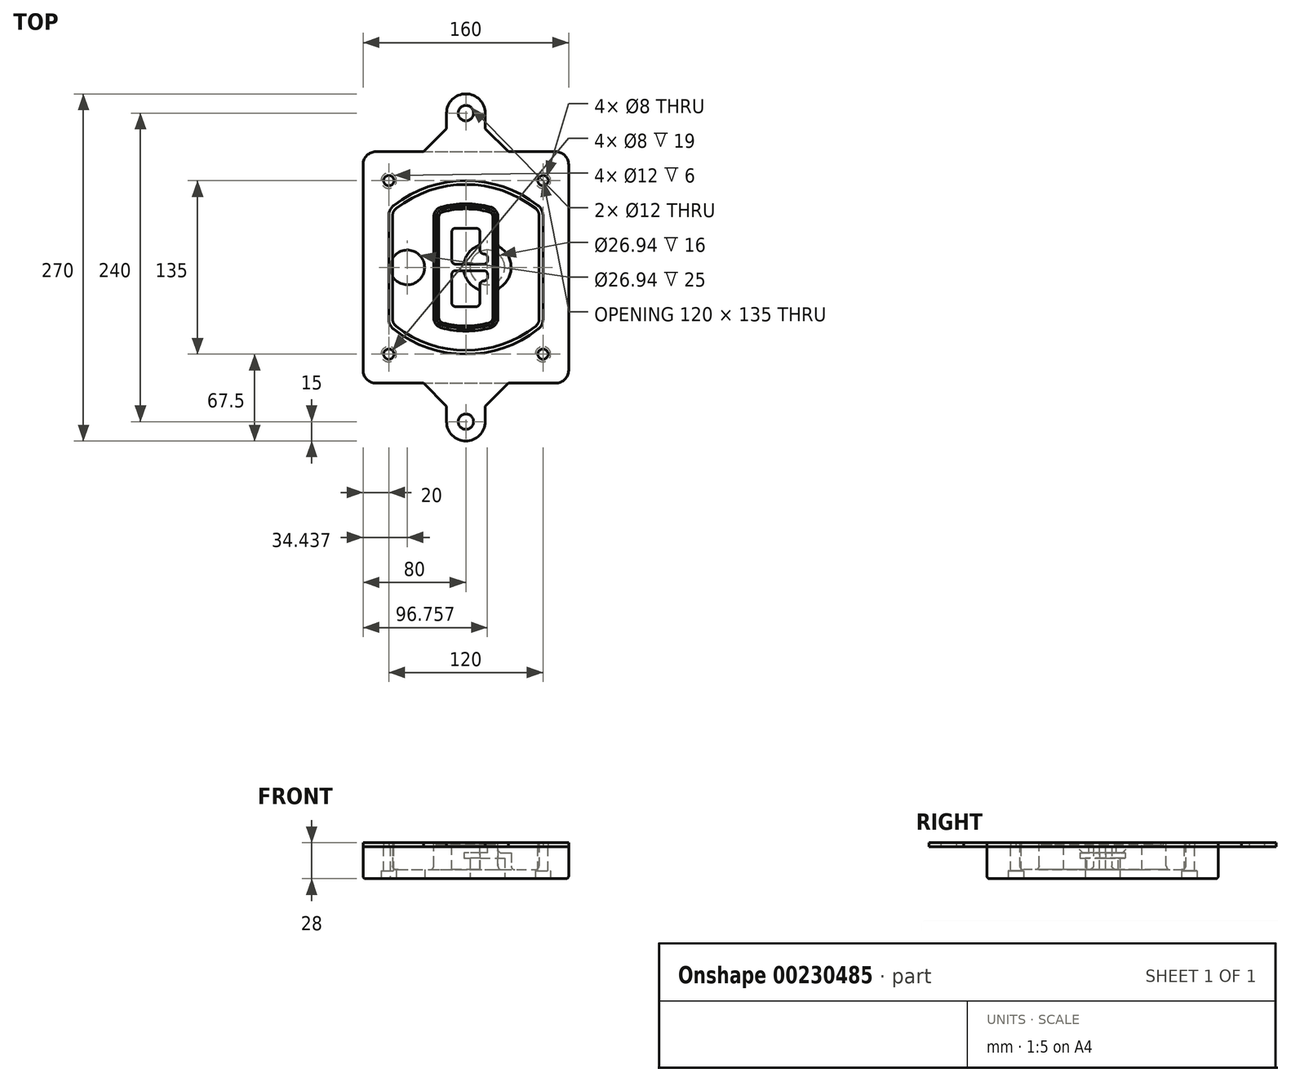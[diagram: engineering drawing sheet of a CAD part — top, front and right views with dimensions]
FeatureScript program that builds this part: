
annotation { "Feature Type Name" : "Feature", "Feature Type Description" : "" }
export const myFeature = defineFeature(function(context is Context, id is Id, definition is map)
    precondition{}
    {
        {
            var Q0;
            Q0=qCreatedBy(makeId("Top.planeOp"),FACE);
            var sketch = newSketch(context, id + "F0", { "sketchPlane" : qUnion([Q0])});
            skPoint(sketch, "E0.rect.middle", {"position": v(0, 0) * mm});
            skLineSegment(sketch, "E1.bottom", {"start": v(-70, -90) * mm, "end": v(70, -90) * mm});
            skLineSegment(sketch, "E1.top", {"start": v(-70, 90) * mm, "end": v(70, 90) * mm});
            skLineSegment(sketch, "E1.left", {"start": v(-80, -80) * mm, "end": v(-80, 80) * mm});
            skLineSegment(sketch, "E1.right", {"start": v(80, -80) * mm, "end": v(80, 80) * mm});
            skLineSegment(sketch, "E2", {"start": v(-80, 90) * mm, "end": v(80, -90) * mm, "construction": true});
            skLineSegment(sketch, "E3", {"start": v(80, 90) * mm, "end": v(-80, -90) * mm, "construction": true});
            skCircle(sketch, "E4", {"center": v(-60, 67.5) * mm, "radius": 4 * mm});
            skCircle(sketch, "E5", {"center": v(60, 67.5) * mm, "radius": 4 * mm});
            skCircle(sketch, "E6", {"center": v(60, -67.5) * mm, "radius": 4 * mm});
            skCircle(sketch, "E7", {"center": v(-60, -67.5) * mm, "radius": 4 * mm});
            skLineSegment(sketch, "E8", {"start": v(-60, 67.5) * mm, "end": v(60, 67.5) * mm, "construction": true});
            skLineSegment(sketch, "E9", {"start": v(60, 67.5) * mm, "end": v(60, -67.5) * mm, "construction": true});
            skLineSegment(sketch, "E10", {"start": v(60, -67.5) * mm, "end": v(-60, -67.5) * mm, "construction": true});
            skLineSegment(sketch, "E11", {"start": v(-60, -67.5) * mm, "end": v(-60, 67.5) * mm, "construction": true});
            skLineSegment(sketch, "E12", {"start": v(-60, 40.3) * mm, "end": v(-60, -40.3) * mm});
            skLineSegment(sketch, "E13", {"start": v(60, 40.3) * mm, "end": v(60, -40.3) * mm});
            skArc(sketch, "E14", {"start": v(56.15, 48.18) * mm, "mid": v(0, 67.5) * mm, "end": v(-56.15, 48.18) * mm});
            skArc(sketch, "E15", {"start": v(-56.15, -48.18) * mm, "mid": v(0, -67.5) * mm, "end": v(56.15, -48.18) * mm});
            skLineSegment(sketch, "E16", {"start": v(-60, 0) * mm, "end": v(60, 0) * mm, "construction": true});
            skPoint(sketch, "E17.visualSharp", {"position": v(-60, -45) * mm});
            skArc(sketch, "E17.filletArc", {"start": v(-60, -40.3) * mm, "mid": v(-58.99, -44.68) * mm, "end": v(-56.15, -48.18) * mm});
            skPoint(sketch, "E18.visualSharp", {"position": v(-60, 45) * mm});
            skArc(sketch, "E18.filletArc", {"start": v(-56.15, 48.18) * mm, "mid": v(-58.99, 44.68) * mm, "end": v(-60, 40.3) * mm});
            skPoint(sketch, "E19.visualSharp", {"position": v(60, 45) * mm});
            skArc(sketch, "E19.filletArc", {"start": v(60, 40.3) * mm, "mid": v(58.99, 44.68) * mm, "end": v(56.15, 48.18) * mm});
            skPoint(sketch, "E20.visualSharp", {"position": v(60, -45) * mm});
            skArc(sketch, "E20.filletArc", {"start": v(56.15, -48.18) * mm, "mid": v(58.99, -44.68) * mm, "end": v(60, -40.3) * mm});
            skPoint(sketch, "E21.visualSharp", {"position": v(-80, 90) * mm});
            skArc(sketch, "E21.filletArc", {"start": v(-70, 90) * mm, "mid": v(-77.07, 87.07) * mm, "end": v(-80, 80) * mm});
            skPoint(sketch, "E22.visualSharp", {"position": v(80, 90) * mm});
            skArc(sketch, "E22.filletArc", {"start": v(80, 80) * mm, "mid": v(77.07, 87.07) * mm, "end": v(70, 90) * mm});
            skPoint(sketch, "E23.visualSharp", {"position": v(80, -90) * mm});
            skArc(sketch, "E23.filletArc", {"start": v(70, -90) * mm, "mid": v(77.07, -87.07) * mm, "end": v(80, -80) * mm});
            skPoint(sketch, "E24.visualSharp", {"position": v(-80, -90) * mm});
            skArc(sketch, "E24.filletArc", {"start": v(-80, -80) * mm, "mid": v(-77.07, -87.07) * mm, "end": v(-70, -90) * mm});
            skArc(sketch, "E25.0", {"start": v(57, 40.3) * mm, "mid": v(56.3, 43.36) * mm, "end": v(54.3, 45.81) * mm});
            skLineSegment(sketch, "E25.1", {"start": v(57, 40.3) * mm, "end": v(57, -40.3) * mm});
            skArc(sketch, "E25.2", {"start": v(54.3, -45.81) * mm, "mid": v(56.3, -43.36) * mm, "end": v(57, -40.3) * mm});
            skArc(sketch, "E25.3", {"start": v(-54.3, -45.81) * mm, "mid": v(0, -64.5) * mm, "end": v(54.3, -45.81) * mm});
            skArc(sketch, "E25.4", {"start": v(-57, -40.3) * mm, "mid": v(-56.3, -43.36) * mm, "end": v(-54.3, -45.81) * mm});
            skArc(sketch, "E25.5", {"start": v(54.3, 45.81) * mm, "mid": v(0, 64.5) * mm, "end": v(-54.3, 45.81) * mm});
            skLineSegment(sketch, "E25.6", {"start": v(-57, 40.3) * mm, "end": v(-57, -40.3) * mm});
            skArc(sketch, "E25.7", {"start": v(-54.3, 45.81) * mm, "mid": v(-56.3, 43.36) * mm, "end": v(-57, 40.3) * mm});
            skArc(sketch, "E26.0", {"start": v(-58.62, 51.33) * mm, "mid": v(-62.58, 46.43) * mm, "end": v(-64, 40.3) * mm});
            skArc(sketch, "E26.1", {"start": v(58.62, 51.33) * mm, "mid": v(0, 71.5) * mm, "end": v(-58.62, 51.33) * mm});
            skArc(sketch, "E26.2", {"start": v(64, 40.3) * mm, "mid": v(62.58, 46.43) * mm, "end": v(58.62, 51.33) * mm});
            skLineSegment(sketch, "E26.3", {"start": v(64, 40.3) * mm, "end": v(64, -40.3) * mm});
            skArc(sketch, "E26.4", {"start": v(58.62, -51.33) * mm, "mid": v(62.58, -46.43) * mm, "end": v(64, -40.3) * mm});
            skLineSegment(sketch, "E26.5", {"start": v(-64, 40.3) * mm, "end": v(-64, -40.3) * mm});
            skArc(sketch, "E26.6", {"start": v(-58.62, -51.33) * mm, "mid": v(0, -71.5) * mm, "end": v(58.62, -51.33) * mm});
            skArc(sketch, "E26.7", {"start": v(-64, -40.3) * mm, "mid": v(-62.58, -46.43) * mm, "end": v(-58.62, -51.33) * mm});
            skSolve(sketch);
        }
        {
            var Q0;
            Q0=makeQuery(id+"F0.imprint","IMPRINT",FACE,{"disambiguationData":[TD([[makeQuery(id+"F0.imprint","IMPRINT",EDGE,{"derivedFrom":sQuery(id+"F0.wireOp",EDGE,"E1.bottom")}),1.0]])]});
            var Q1;
            Q1=makeQuery(id+"F0.imprint","IMPRINT",FACE,{"disambiguationData":[TD([[makeQuery(id+"F0.imprint","IMPRINT",EDGE,{"derivedFrom":sQuery(id+"F0.wireOp",EDGE,"E12")}),1.0]])]});
            var Q2;
            Q2=makeQuery(id+"F0.imprint","IMPRINT",FACE,{"disambiguationData":[TD([[makeQuery(id+"F0.imprint","IMPRINT",EDGE,{"derivedFrom":sQuery(id+"F0.wireOp",EDGE,"E25.0")}),1.0]])]});
            var Q3;
            Q3=makeQuery(id+"F0.imprint","IMPRINT",FACE,{"disambiguationData":[TD([[makeQuery(id+"F0.imprint","IMPRINT",EDGE,{"derivedFrom":sQuery(id+"F0.wireOp",EDGE,"E12")}),-1.0]])]});
            extrude(context, id + "F1", {"entities" : qUnion([Q0, Q1, Q2, Q3]), "oppositeDirection" : true, "depth" : 25 * mm});
        }
        {
            var Q0;
            Q0=makeQuery(id+"F0.imprint","IMPRINT",FACE,{"disambiguationData":[TD([[makeQuery(id+"F0.imprint","IMPRINT",EDGE,{"derivedFrom":sQuery(id+"F0.wireOp",EDGE,"E12")}),1.0]])]});
            extrude(context, id + "F2", {"entities" : qUnion([Q0]), "operationType" : NewBodyOperationType.ADD, "depth" : 3 * mm});
        }
        {
            var Q0;
            Q0=makeQuery(id+"F0.imprint","IMPRINT",FACE,{"disambiguationData":[TD([[makeQuery(id+"F0.imprint","IMPRINT",EDGE,{"derivedFrom":sQuery(id+"F0.wireOp",EDGE,"E25.0")}),1.0]])]});
            extrude(context, id + "F3", {"entities" : qUnion([Q0]), "operationType" : NewBodyOperationType.REMOVE, "oppositeDirection" : true, "depth" : 18 * mm});
        }
        {
            var Q0;
            Q0=makeQuery(id+"F2.opExtrude","CAP_FACE",FACE,{"disambiguationData":[OSD([sQuery(id+"F0.wireOp",EDGE,"E12"),sQuery(id+"F0.wireOp",EDGE,"E13"),sQuery(id+"F0.wireOp",EDGE,"E14"),sQuery(id+"F0.wireOp",EDGE,"E15"),sQuery(id+"F0.wireOp",EDGE,"E17.filletArc"),sQuery(id+"F0.wireOp",EDGE,"E18.filletArc"),sQuery(id+"F0.wireOp",EDGE,"E19.filletArc"),sQuery(id+"F0.wireOp",EDGE,"E20.filletArc"),sQuery(id+"F0.wireOp",EDGE,"E25.0"),sQuery(id+"F0.wireOp",EDGE,"E25.1"),sQuery(id+"F0.wireOp",EDGE,"E25.2"),sQuery(id+"F0.wireOp",EDGE,"E25.3"),sQuery(id+"F0.wireOp",EDGE,"E25.4"),sQuery(id+"F0.wireOp",EDGE,"E25.5"),sQuery(id+"F0.wireOp",EDGE,"E25.6"),sQuery(id+"F0.wireOp",EDGE,"E25.7")])],"isStart":false});
            var sketch = newSketch(context, id + "F4", { "sketchPlane" : qUnion([Q0])});
            skArc(sketch, "E27.0", {"start": v(-19.08, -46.97) * mm, "mid": v(0, -49.5) * mm, "end": v(19.08, -46.97) * mm});
            skArc(sketch, "E28.0", {"start": v(19.08, 46.97) * mm, "mid": v(0, 49.5) * mm, "end": v(-19.08, 46.97) * mm});
            skLineSegment(sketch, "E29", {"start": v(-25, 39.25) * mm, "end": v(-25, -39.25) * mm});
            skLineSegment(sketch, "E30", {"start": v(25, 39.25) * mm, "end": v(25, -39.25) * mm});
            skLineSegment(sketch, "E31", {"start": v(-25, 45.1) * mm, "end": v(25, 45.1) * mm, "construction": true});
            skLineSegment(sketch, "E32", {"start": v(-25, -45.1) * mm, "end": v(25, -45.1) * mm, "construction": true});
            skPoint(sketch, "E33.visualSharp", {"position": v(-25, 45.1) * mm});
            skArc(sketch, "E33.filletArc", {"start": v(-19.08, 46.97) * mm, "mid": v(-23.35, 44.11) * mm, "end": v(-25, 39.25) * mm});
            skPoint(sketch, "E34.visualSharp", {"position": v(25, 45.1) * mm});
            skArc(sketch, "E34.filletArc", {"start": v(25, 39.25) * mm, "mid": v(23.35, 44.11) * mm, "end": v(19.08, 46.97) * mm});
            skPoint(sketch, "E35.visualSharp", {"position": v(25, -45.1) * mm});
            skArc(sketch, "E35.filletArc", {"start": v(19.08, -46.97) * mm, "mid": v(23.35, -44.11) * mm, "end": v(25, -39.25) * mm});
            skPoint(sketch, "E36.visualSharp", {"position": v(-25, -45.1) * mm});
            skArc(sketch, "E36.filletArc", {"start": v(-25, -39.25) * mm, "mid": v(-23.35, -44.11) * mm, "end": v(-19.08, -46.97) * mm});
            skArc(sketch, "E37.0", {"start": v(54.3, 45.81) * mm, "mid": v(0, 64.5) * mm, "end": v(-54.3, 45.81) * mm});
            skArc(sketch, "E37.1", {"start": v(-54.3, 45.81) * mm, "mid": v(-56.3, 43.36) * mm, "end": v(-57, 40.3) * mm});
            skLineSegment(sketch, "E37.2", {"start": v(-57, 40.3) * mm, "end": v(-57, -40.3) * mm});
            skArc(sketch, "E37.3", {"start": v(-57, -40.3) * mm, "mid": v(-56.3, -43.36) * mm, "end": v(-54.3, -45.81) * mm});
            skArc(sketch, "E37.4", {"start": v(-54.3, -45.81) * mm, "mid": v(0, -64.5) * mm, "end": v(54.3, -45.81) * mm});
            skArc(sketch, "E37.5", {"start": v(54.3, -45.81) * mm, "mid": v(56.3, -43.36) * mm, "end": v(57, -40.3) * mm});
            skLineSegment(sketch, "E37.6", {"start": v(57, 40.3) * mm, "end": v(57, -40.3) * mm});
            skArc(sketch, "E37.7", {"start": v(57, 40.3) * mm, "mid": v(56.3, 43.36) * mm, "end": v(54.3, 45.81) * mm});
            skLineSegment(sketch, "E38.0", {"start": v(23, 39.25) * mm, "end": v(23, -39.25) * mm});
            skArc(sketch, "E38.1", {"start": v(18.56, -45.04) * mm, "mid": v(21.76, -42.9) * mm, "end": v(23, -39.25) * mm});
            skArc(sketch, "E38.2", {"start": v(-18.56, -45.04) * mm, "mid": v(0, -47.5) * mm, "end": v(18.56, -45.04) * mm});
            skArc(sketch, "E38.3", {"start": v(-23, -39.25) * mm, "mid": v(-21.76, -42.9) * mm, "end": v(-18.56, -45.04) * mm});
            skLineSegment(sketch, "E38.4", {"start": v(-23, 39.25) * mm, "end": v(-23, -39.25) * mm});
            skArc(sketch, "E38.5", {"start": v(23, 39.25) * mm, "mid": v(21.76, 42.9) * mm, "end": v(18.56, 45.04) * mm});
            skArc(sketch, "E38.6", {"start": v(-18.56, 45.04) * mm, "mid": v(-21.76, 42.9) * mm, "end": v(-23, 39.25) * mm});
            skArc(sketch, "E38.7", {"start": v(18.56, 45.04) * mm, "mid": v(0, 47.5) * mm, "end": v(-18.56, 45.04) * mm});
            skArc(sketch, "E39.0", {"start": v(21, 39.25) * mm, "mid": v(20.18, 41.68) * mm, "end": v(18.04, 43.1) * mm});
            skLineSegment(sketch, "E39.1", {"start": v(21, 39.25) * mm, "end": v(21, -39.25) * mm});
            skArc(sketch, "E39.2", {"start": v(18.04, -43.1) * mm, "mid": v(20.18, -41.68) * mm, "end": v(21, -39.25) * mm});
            skArc(sketch, "E39.3", {"start": v(-18.04, -43.1) * mm, "mid": v(0, -45.5) * mm, "end": v(18.04, -43.1) * mm});
            skArc(sketch, "E39.4", {"start": v(-21, -39.25) * mm, "mid": v(-20.18, -41.68) * mm, "end": v(-18.04, -43.1) * mm});
            skArc(sketch, "E39.5", {"start": v(18.04, 43.1) * mm, "mid": v(0, 45.5) * mm, "end": v(-18.04, 43.1) * mm});
            skLineSegment(sketch, "E39.6", {"start": v(-21, 39.25) * mm, "end": v(-21, -39.25) * mm});
            skArc(sketch, "E39.7", {"start": v(-18.04, 43.1) * mm, "mid": v(-20.18, 41.68) * mm, "end": v(-21, 39.25) * mm});
            skLineSegment(sketch, "E40", {"start": v(-25, 0) * mm, "end": v(25, 0) * mm, "construction": true});
            skLineSegment(sketch, "E41", {"start": v(-11, 5.5) * mm, "end": v(-11, 27.5) * mm});
            skLineSegment(sketch, "E42", {"start": v(-8, 30.5) * mm, "end": v(8, 30.5) * mm});
            skLineSegment(sketch, "E43", {"start": v(11, 27.5) * mm, "end": v(11, 13.5) * mm});
            skLineSegment(sketch, "E44", {"start": v(14, 10.5) * mm, "end": v(14, 10.5) * mm});
            skLineSegment(sketch, "E45", {"start": v(17, 7.5) * mm, "end": v(17, 5.5) * mm});
            skLineSegment(sketch, "E46", {"start": v(14, 2.5) * mm, "end": v(-8, 2.5) * mm});
            skPoint(sketch, "E47.visualSharp", {"position": v(-11, 30.5) * mm});
            skArc(sketch, "E47.filletArc", {"start": v(-8, 30.5) * mm, "mid": v(-10.12, 29.62) * mm, "end": v(-11, 27.5) * mm});
            skPoint(sketch, "E48.visualSharp", {"position": v(11, 30.5) * mm});
            skArc(sketch, "E48.filletArc", {"start": v(11, 27.5) * mm, "mid": v(10.12, 29.62) * mm, "end": v(8, 30.5) * mm});
            skPoint(sketch, "E49.visualSharp", {"position": v(11, 10.5) * mm});
            skArc(sketch, "E49.filletArc", {"start": v(11, 13.5) * mm, "mid": v(11.88, 11.38) * mm, "end": v(14, 10.5) * mm});
            skPoint(sketch, "E50.visualSharp", {"position": v(17, 10.5) * mm});
            skArc(sketch, "E50.filletArc", {"start": v(17, 7.5) * mm, "mid": v(16.12, 9.62) * mm, "end": v(14, 10.5) * mm});
            skPoint(sketch, "E51.visualSharp", {"position": v(17, 2.5) * mm});
            skArc(sketch, "E51.filletArc", {"start": v(14, 2.5) * mm, "mid": v(16.12, 3.38) * mm, "end": v(17, 5.5) * mm});
            skPoint(sketch, "E52.visualSharp", {"position": v(-11, 2.5) * mm});
            skArc(sketch, "E52.filletArc", {"start": v(-11, 5.5) * mm, "mid": v(-10.12, 3.38) * mm, "end": v(-8, 2.5) * mm});
            skLineSegment(sketch, "E53.0.MirrorCS", {"start": v(14, -2.5) * mm, "end": v(-8, -2.5) * mm});
            skArc(sketch, "E54.0.MirrorCS", {"start": v(-11, -5.5) * mm, "mid": v(-10.12, -3.38) * mm, "end": v(-8, -2.5) * mm});
            skLineSegment(sketch, "E55.0.MirrorCS", {"start": v(-11, -5.5) * mm, "end": v(-11, -27.5) * mm});
            skArc(sketch, "E56.0.MirrorCS", {"start": v(-8, -30.5) * mm, "mid": v(-10.12, -29.62) * mm, "end": v(-11, -27.5) * mm});
            skLineSegment(sketch, "E57.0.MirrorCS", {"start": v(-8, -30.5) * mm, "end": v(8, -30.5) * mm});
            skArc(sketch, "E58.0.MirrorCS", {"start": v(11, -27.5) * mm, "mid": v(10.12, -29.62) * mm, "end": v(8, -30.5) * mm});
            skLineSegment(sketch, "E59.0.MirrorCS", {"start": v(11, -27.5) * mm, "end": v(11, -13.5) * mm});
            skArc(sketch, "E60.0.MirrorCS", {"start": v(11, -13.5) * mm, "mid": v(11.88, -11.38) * mm, "end": v(14, -10.5) * mm});
            skArc(sketch, "E61.0.MirrorCS", {"start": v(17, -7.5) * mm, "mid": v(16.12, -9.62) * mm, "end": v(14, -10.5) * mm});
            skLineSegment(sketch, "E62.0.MirrorCS", {"start": v(17, -7.5) * mm, "end": v(17, -5.5) * mm});
            skArc(sketch, "E63.0.MirrorCS", {"start": v(14, -2.5) * mm, "mid": v(16.12, -3.38) * mm, "end": v(17, -5.5) * mm});
            skSolve(sketch);
        }
        {
            var Q0;
            Q0=makeQuery(id+"F4.imprint","IMPRINT",FACE,{"disambiguationData":[TD([[makeQuery(id+"F4.imprint","IMPRINT",EDGE,{"derivedFrom":sQuery(id+"F4.wireOp",EDGE,"E27.0")}),1.0]])]});
            var Q1;
            Q1=makeQuery(id+"F4.imprint","IMPRINT",FACE,{"disambiguationData":[TD([[makeQuery(id+"F4.imprint","IMPRINT",EDGE,{"derivedFrom":sQuery(id+"F4.wireOp",EDGE,"E38.0")}),-1.0]])]});
            var Q2;
            Q2=makeQuery(id+"F4.imprint","IMPRINT",FACE,{"disambiguationData":[TD([[makeQuery(id+"F4.imprint","IMPRINT",EDGE,{"derivedFrom":sQuery(id+"F4.wireOp",EDGE,"E39.0")}),1.0]])]});
            extrude(context, id + "F5", {"entities" : qUnion([Q0, Q1, Q2]), "operationType" : NewBodyOperationType.ADD, "endBound" : BoundingType.UP_TO_NEXT, "oppositeDirection" : true, "depth" : 25 * mm});
        }
        {
            var Q0;
            Q0=makeQuery(id+"F4.imprint","IMPRINT",FACE,{"disambiguationData":[TD([[makeQuery(id+"F4.imprint","IMPRINT",EDGE,{"derivedFrom":sQuery(id+"F4.wireOp",EDGE,"E38.0")}),-1.0]])]});
            extrude(context, id + "F6", {"entities" : qUnion([Q0]), "operationType" : NewBodyOperationType.REMOVE, "oppositeDirection" : true, "depth" : 2 * mm});
        }
        {
            var Q0;
            Q0=makeQuery(id+"F1.opExtrude","CAP_FACE",FACE,{"disambiguationData":[OSD([sQuery(id+"F0.wireOp",EDGE,"E1.bottom"),sQuery(id+"F0.wireOp",EDGE,"E1.top"),sQuery(id+"F0.wireOp",EDGE,"E1.left"),sQuery(id+"F0.wireOp",EDGE,"E1.right"),sQuery(id+"F0.wireOp",EDGE,"E4"),sQuery(id+"F0.wireOp",EDGE,"E5"),sQuery(id+"F0.wireOp",EDGE,"E6"),sQuery(id+"F0.wireOp",EDGE,"E7"),sQuery(id+"F0.wireOp",EDGE,"E21.filletArc"),sQuery(id+"F0.wireOp",EDGE,"E22.filletArc"),sQuery(id+"F0.wireOp",EDGE,"E23.filletArc"),sQuery(id+"F0.wireOp",EDGE,"E24.filletArc")])],"isStart":false});
            var sketch = newSketch(context, id + "F7", { "sketchPlane" : qUnion([Q0])});
            skCircle(sketch, "E64", {"center": v(16.76, 0) * mm, "radius": 13.47 * mm});
            skCircle(sketch, "E65", {"center": v(-45.56, 0) * mm, "radius": 13.47 * mm});
            skLineSegment(sketch, "E66", {"start": v(80, 0) * mm, "end": v(-80, 0) * mm});
            skCircle(sketch, "E67", {"center": v(16.76, 0) * mm, "radius": 18.47 * mm});
            skCircle(sketch, "E68", {"center": v(60, -67.5) * mm, "radius": 6 * mm});
            skCircle(sketch, "E69", {"center": v(-60, -67.5) * mm, "radius": 6 * mm});
            skCircle(sketch, "E70", {"center": v(-60, 67.5) * mm, "radius": 6 * mm});
            skCircle(sketch, "E71", {"center": v(60, 67.5) * mm, "radius": 6 * mm});
            skSolve(sketch);
        }
        {
            var Q0;
            {var subQ1=sQuery(id+"F7.wireOp",EDGE,"E66");var subQ4=sQuery(id+"F7.wireOp",EDGE,"E64");var subQ6=makeQuery(id+"F7.imprint","INTERSECT",VERTEX,{"disambiguationData":[OD(0.0)],"derivedFrom":[subQ4,subQ1]});Q0=makeQuery(id+"F7.imprint","IMPRINT",FACE,{"disambiguationData":[TD([[makeQuery(id+"F7.imprint","IMPRINT",EDGE,{"disambiguationData":[TD([[subQ6,-1.0]])],"derivedFrom":subQ4}),-1.0]])]});}
            var Q1;
            {var subQ0=sQuery(id+"F7.wireOp",EDGE,"E66");var subQ1=sQuery(id+"F7.wireOp",EDGE,"E64");var subQ3=makeQuery(id+"F7.imprint","INTERSECT",VERTEX,{"disambiguationData":[OD(0.0)],"derivedFrom":[subQ1,subQ0]});Q1=makeQuery(id+"F7.imprint","IMPRINT",FACE,{"disambiguationData":[TD([[makeQuery(id+"F7.imprint","IMPRINT",EDGE,{"disambiguationData":[TD([[subQ3,-1.0]])],"derivedFrom":subQ1}),1.0]])]});}
            var Q2;
            {var subQ0=sQuery(id+"F7.wireOp",EDGE,"E66");var subQ1=sQuery(id+"F7.wireOp",EDGE,"E64");var subQ3=makeQuery(id+"F7.imprint","INTERSECT",VERTEX,{"disambiguationData":[OD(0.0)],"derivedFrom":[subQ1,subQ0]});Q2=makeQuery(id+"F7.imprint","IMPRINT",FACE,{"disambiguationData":[TD([[makeQuery(id+"F7.imprint","IMPRINT",EDGE,{"disambiguationData":[TD([[subQ3,1.0]])],"derivedFrom":subQ1}),1.0]])]});}
            var Q3;
            {var subQ1=sQuery(id+"F7.wireOp",EDGE,"E66");var subQ4=sQuery(id+"F7.wireOp",EDGE,"E64");var subQ6=makeQuery(id+"F7.imprint","INTERSECT",VERTEX,{"disambiguationData":[OD(0.0)],"derivedFrom":[subQ4,subQ1]});Q3=makeQuery(id+"F7.imprint","IMPRINT",FACE,{"disambiguationData":[TD([[makeQuery(id+"F7.imprint","IMPRINT",EDGE,{"disambiguationData":[TD([[subQ6,1.0]])],"derivedFrom":subQ4}),-1.0]])]});}
            extrude(context, id + "F8", {"entities" : qUnion([Q0, Q1, Q2, Q3]), "operationType" : NewBodyOperationType.ADD, "oppositeDirection" : true, "depth" : 20 * mm});
        }
        {
            var Q0;
            {var subQ0=sQuery(id+"F7.wireOp",EDGE,"E66");var subQ1=sQuery(id+"F7.wireOp",EDGE,"E64");var subQ3=makeQuery(id+"F7.imprint","INTERSECT",VERTEX,{"disambiguationData":[OD(0.0)],"derivedFrom":[subQ1,subQ0]});Q0=makeQuery(id+"F7.imprint","IMPRINT",FACE,{"disambiguationData":[TD([[makeQuery(id+"F7.imprint","IMPRINT",EDGE,{"disambiguationData":[TD([[subQ3,-1.0]])],"derivedFrom":subQ1}),1.0]])]});}
            var Q1;
            {var subQ0=sQuery(id+"F7.wireOp",EDGE,"E66");var subQ1=sQuery(id+"F7.wireOp",EDGE,"E64");var subQ3=makeQuery(id+"F7.imprint","INTERSECT",VERTEX,{"disambiguationData":[OD(0.0)],"derivedFrom":[subQ1,subQ0]});Q1=makeQuery(id+"F7.imprint","IMPRINT",FACE,{"disambiguationData":[TD([[makeQuery(id+"F7.imprint","IMPRINT",EDGE,{"disambiguationData":[TD([[subQ3,1.0]])],"derivedFrom":subQ1}),1.0]])]});}
            extrude(context, id + "F9", {"entities" : qUnion([Q0, Q1]), "operationType" : NewBodyOperationType.REMOVE, "oppositeDirection" : true, "depth" : 16 * mm});
        }
        {
            var Q0;
            {var subQ0=sQuery(id+"F7.wireOp",EDGE,"E66");var subQ1=sQuery(id+"F7.wireOp",EDGE,"E65");var subQ3=makeQuery(id+"F7.imprint","INTERSECT",VERTEX,{"disambiguationData":[OD(0.0)],"derivedFrom":[subQ1,subQ0]});Q0=makeQuery(id+"F7.imprint","IMPRINT",FACE,{"disambiguationData":[TD([[makeQuery(id+"F7.imprint","IMPRINT",EDGE,{"disambiguationData":[TD([[subQ3,-1.0]])],"derivedFrom":subQ1}),1.0]])]});}
            var Q1;
            {var subQ0=sQuery(id+"F7.wireOp",EDGE,"E66");var subQ1=sQuery(id+"F7.wireOp",EDGE,"E65");var subQ3=makeQuery(id+"F7.imprint","INTERSECT",VERTEX,{"disambiguationData":[OD(0.0)],"derivedFrom":[subQ1,subQ0]});Q1=makeQuery(id+"F7.imprint","IMPRINT",FACE,{"disambiguationData":[TD([[makeQuery(id+"F7.imprint","IMPRINT",EDGE,{"disambiguationData":[TD([[subQ3,1.0]])],"derivedFrom":subQ1}),1.0]])]});}
            extrude(context, id + "F10", {"entities" : qUnion([Q0, Q1]), "operationType" : NewBodyOperationType.REMOVE, "oppositeDirection" : true, "depth" : 25 * mm});
        }
        {
            var Q0;
            Q0=makeQuery(id+"F7.imprint","IMPRINT",FACE,{"disambiguationData":[TD([[makeQuery(id+"F7.imprint","IMPRINT",EDGE,{"derivedFrom":sQuery(id+"F7.wireOp",EDGE,"E68")}),1.0]])]});
            var Q1;
            Q1=makeQuery(id+"F7.imprint","IMPRINT",FACE,{"disambiguationData":[TD([[makeQuery(id+"F7.imprint","IMPRINT",EDGE,{"derivedFrom":makeQuery(id+"F1.opExtrude","CAP_EDGE",EDGE,{"disambiguationData":[OSD([sQuery(id+"F0.wireOp",EDGE,"E5")])],"isStart":false})}),-1.0]])]});
            var Q2;
            Q2=makeQuery(id+"F7.imprint","IMPRINT",FACE,{"disambiguationData":[TD([[makeQuery(id+"F7.imprint","IMPRINT",EDGE,{"derivedFrom":sQuery(id+"F7.wireOp",EDGE,"E69")}),1.0]])]});
            var Q3;
            Q3=makeQuery(id+"F7.imprint","IMPRINT",FACE,{"disambiguationData":[TD([[makeQuery(id+"F7.imprint","IMPRINT",EDGE,{"derivedFrom":makeQuery(id+"F1.opExtrude","CAP_EDGE",EDGE,{"disambiguationData":[OSD([sQuery(id+"F0.wireOp",EDGE,"E4")])],"isStart":false})}),-1.0]])]});
            var Q4;
            Q4=makeQuery(id+"F7.imprint","IMPRINT",FACE,{"disambiguationData":[TD([[makeQuery(id+"F7.imprint","IMPRINT",EDGE,{"derivedFrom":sQuery(id+"F7.wireOp",EDGE,"E70")}),1.0]])]});
            var Q5;
            Q5=makeQuery(id+"F7.imprint","IMPRINT",FACE,{"disambiguationData":[TD([[makeQuery(id+"F7.imprint","IMPRINT",EDGE,{"derivedFrom":makeQuery(id+"F1.opExtrude","CAP_EDGE",EDGE,{"disambiguationData":[OSD([sQuery(id+"F0.wireOp",EDGE,"E7")])],"isStart":false})}),-1.0]])]});
            var Q6;
            Q6=makeQuery(id+"F7.imprint","IMPRINT",FACE,{"disambiguationData":[TD([[makeQuery(id+"F7.imprint","IMPRINT",EDGE,{"derivedFrom":sQuery(id+"F7.wireOp",EDGE,"E71")}),1.0]])]});
            var Q7;
            Q7=makeQuery(id+"F7.imprint","IMPRINT",FACE,{"disambiguationData":[TD([[makeQuery(id+"F7.imprint","IMPRINT",EDGE,{"derivedFrom":makeQuery(id+"F1.opExtrude","CAP_EDGE",EDGE,{"disambiguationData":[OSD([sQuery(id+"F0.wireOp",EDGE,"E6")])],"isStart":false})}),-1.0]])]});
            extrude(context, id + "F11", {"entities" : qUnion([Q0, Q1, Q2, Q3, Q4, Q5, Q6, Q7]), "operationType" : NewBodyOperationType.REMOVE, "oppositeDirection" : true, "depth" : 6 * mm});
        }
        {
            var Q0;
            Q0=makeQuery(id+"F9.boolean.opBoolean","COPY",FACE,{"derivedFrom":makeQuery(id+"F9.opExtrude","CAP_FACE",FACE,{"disambiguationData":[OSD([sQuery(id+"F7.wireOp",EDGE,"E64")])],"isStart":false})});
            var sketch = newSketch(context, id + "F12", { "sketchPlane" : qUnion([Q0])});
            skArc(sketch, "E72.0", {"start": v(11, 17.55) * mm, "mid": v(2.57, 11.82) * mm, "end": v(-1.54, 2.5) * mm});
            skArc(sketch, "E72.1", {"start": v(-1.54, -2.5) * mm, "mid": v(2.57, -11.82) * mm, "end": v(11, -17.55) * mm});
            skLineSegment(sketch, "E73", {"start": v(-1.54, -2.5) * mm, "end": v(14, -2.5) * mm});
            skLineSegment(sketch, "E74.0", {"start": v(14, 2.5) * mm, "end": v(-1.54, 2.5) * mm});
            skArc(sketch, "E74.1", {"start": v(14, 2.5) * mm, "mid": v(16.12, 3.38) * mm, "end": v(17, 5.5) * mm});
            skLineSegment(sketch, "E74.2", {"start": v(17, 7.5) * mm, "end": v(17, 5.5) * mm});
            skArc(sketch, "E74.3", {"start": v(17, 7.5) * mm, "mid": v(16.12, 9.62) * mm, "end": v(14, 10.5) * mm});
            skArc(sketch, "E74.4", {"start": v(11, 13.5) * mm, "mid": v(11.88, 11.38) * mm, "end": v(14, 10.5) * mm});
            skLineSegment(sketch, "E74.5", {"start": v(11, 17.55) * mm, "end": v(11, 13.5) * mm});
            skLineSegment(sketch, "E74.7", {"start": v(14, -2.5) * mm, "end": v(-1.54, -2.5) * mm});
            skArc(sketch, "E74.8", {"start": v(14, -2.5) * mm, "mid": v(16.12, -3.38) * mm, "end": v(17, -5.5) * mm});
            skLineSegment(sketch, "E74.9", {"start": v(17, -7.5) * mm, "end": v(17, -5.5) * mm});
            skArc(sketch, "E74.10", {"start": v(17, -7.5) * mm, "mid": v(16.12, -9.62) * mm, "end": v(14, -10.5) * mm});
            skArc(sketch, "E74.11", {"start": v(11, -13.5) * mm, "mid": v(11.88, -11.38) * mm, "end": v(14, -10.5) * mm});
            skLineSegment(sketch, "E74.12", {"start": v(11, -17.55) * mm, "end": v(11, -13.5) * mm});
            skPoint(sketch, "E75.orphan", {"position": v(11, -27.5) * mm});
            skPoint(sketch, "E76.orphan", {"position": v(-8, -2.5) * mm});
            skPoint(sketch, "E77.orphan", {"position": v(-8, 2.5) * mm});
            skPoint(sketch, "E78.orphan", {"position": v(11, 27.5) * mm});
            skSolve(sketch);
        }
        {
            var Q0;
            {var subQ7=sQuery(id+"F12.wireOp",EDGE,"E72.0");var subQ14=sQuery(id+"F12.wireOp",EDGE,"E72.1");var subQ16=sQuery(id+"F12.wireOp",EDGE,"E74.1");var subQ18=sQuery(id+"F12.wireOp",EDGE,"E74.8");Q0=qUnion([makeQuery(id+"F12.imprint","IMPRINT",FACE,{"disambiguationData":[TD([[makeQuery(id+"F12.imprint","IMPRINT",EDGE,{"derivedFrom":subQ7}),1.0]])]}),makeQuery(id+"F12.imprint","IMPRINT",FACE,{"disambiguationData":[TD([[makeQuery(id+"F12.imprint","IMPRINT",EDGE,{"derivedFrom":subQ14}),1.0]])]}),makeQuery(id+"F12.imprint","IMPRINT",FACE,{"disambiguationData":[TD([[makeQuery(id+"F12.imprint","IMPRINT",EDGE,{"derivedFrom":subQ16}),1.0]])]}),makeQuery(id+"F12.imprint","IMPRINT",FACE,{"disambiguationData":[TD([[makeQuery(id+"F12.imprint","IMPRINT",EDGE,{"derivedFrom":subQ18}),-1.0]])]})]);}
            var Q1;
            Q1=makeQuery(id+"F5.boolean.opBoolean","SPLIT",FACE,{"disambiguationData":[TD([makeQuery(id+"F5.opExtrude","SWEPT_FACE",FACE,{"disambiguationData":[OSD([sQuery(id+"F4.wireOp",EDGE,"E41")])]})])],"derivedFrom":makeQuery(id+"F3.boolean.opBoolean","COPY",FACE,{"derivedFrom":makeQuery(id+"F3.opExtrude","CAP_FACE",FACE,{"disambiguationData":[OSD([sQuery(id+"F0.wireOp",EDGE,"E25.0"),sQuery(id+"F0.wireOp",EDGE,"E25.1"),sQuery(id+"F0.wireOp",EDGE,"E25.2"),sQuery(id+"F0.wireOp",EDGE,"E25.3"),sQuery(id+"F0.wireOp",EDGE,"E25.4"),sQuery(id+"F0.wireOp",EDGE,"E25.5"),sQuery(id+"F0.wireOp",EDGE,"E25.6"),sQuery(id+"F0.wireOp",EDGE,"E25.7")])],"isStart":false})})});
            extrude(context, id + "F13", {"entities" : qUnion([Q0]), "operationType" : NewBodyOperationType.REMOVE, "endBound" : BoundingType.UP_TO_SURFACE, "endBoundEntityFace" : qUnion([Q1]), "depth" : 25 * mm});
        }
        {
            var Q0;
            Q0=makeQuery(id+"F3.boolean.opBoolean","COPY",EDGE,{"derivedFrom":makeQuery(id+"F3.opExtrude","CAP_EDGE",EDGE,{"disambiguationData":[OSD([sQuery(id+"F0.wireOp",EDGE,"E25.6")])],"isStart":false})});
            var Q1;
            Q1=makeQuery(id+"F8.boolean.opBoolean","INTERSECT",EDGE,{"derivedFrom":[makeQuery(id+"F5.opExtrude","SWEPT_FACE",FACE,{"disambiguationData":[OSD([sQuery(id+"F4.wireOp",EDGE,"E30")])]}),makeQuery(id+"F8.opExtrude","CAP_FACE",FACE,{"disambiguationData":[OSD([sQuery(id+"F7.wireOp",EDGE,"E67")])],"isStart":false})]});
            var Q2;
            Q2=makeQuery(id+"F8.boolean.opBoolean","INTERSECT",EDGE,{"disambiguationData":[OD(1.0)],"derivedFrom":[makeQuery(id+"F5.opExtrude","SWEPT_FACE",FACE,{"disambiguationData":[OSD([sQuery(id+"F4.wireOp",EDGE,"E30")])]}),makeQuery(id+"F8.opExtrude","SWEPT_FACE",FACE,{"disambiguationData":[OSD([sQuery(id+"F7.wireOp",EDGE,"E67")])]})]});
            var Q3;
            {var subQ0=sQuery(id+"F4.wireOp",EDGE,"E30");Q3=makeQuery(id+"F8.boolean.opBoolean","SPLIT",EDGE,{"disambiguationData":[TD([makeQuery(id+"F5.opExtrude","SWEPT_FACE",FACE,{"disambiguationData":[OSD([sQuery(id+"F4.wireOp",EDGE,"E35.filletArc")])]})])],"derivedFrom":makeQuery(id+"F5.opExtrude","CAP_EDGE",EDGE,{"disambiguationData":[OSD([subQ0])],"isStart":false})});}
            var Q4;
            {var subQ0=sQuery(id+"F0.wireOp",EDGE,"E25.7");var subQ1=sQuery(id+"F0.wireOp",EDGE,"E25.1");var subQ2=sQuery(id+"F0.wireOp",EDGE,"E25.6");var subQ3=sQuery(id+"F0.wireOp",EDGE,"E25.5");var subQ4=sQuery(id+"F0.wireOp",EDGE,"E25.4");var subQ5=sQuery(id+"F0.wireOp",EDGE,"E25.0");var subQ6=sQuery(id+"F0.wireOp",EDGE,"E25.2");var subQ7=sQuery(id+"F0.wireOp",EDGE,"E25.3");Q4=makeQuery(id+"F8.boolean.opBoolean","INTERSECT",EDGE,{"derivedFrom":[makeQuery(id+"F5.boolean.opBoolean","SPLIT",FACE,{"disambiguationData":[TD([makeQuery(id+"F2.opExtrude","SWEPT_FACE",FACE,{"disambiguationData":[OSD([subQ5])]})])],"derivedFrom":makeQuery(id+"F3.boolean.opBoolean","COPY",FACE,{"derivedFrom":makeQuery(id+"F3.opExtrude","CAP_FACE",FACE,{"disambiguationData":[OSD([subQ5,subQ1,subQ6,subQ7,subQ4,subQ3,subQ2,subQ0])],"isStart":false})})}),makeQuery(id+"F8.opExtrude","SWEPT_FACE",FACE,{"disambiguationData":[OSD([sQuery(id+"F7.wireOp",EDGE,"E67")])]})]});}
            var Q5;
            Q5=makeQuery(id+"F8.boolean.opBoolean","INTERSECT",EDGE,{"disambiguationData":[OD(0.0)],"derivedFrom":[makeQuery(id+"F5.opExtrude","SWEPT_FACE",FACE,{"disambiguationData":[OSD([sQuery(id+"F4.wireOp",EDGE,"E30")])]}),makeQuery(id+"F8.opExtrude","SWEPT_FACE",FACE,{"disambiguationData":[OSD([sQuery(id+"F7.wireOp",EDGE,"E67")])]})]});
            fillet(context, id + "F14", {"entities" : qUnion([Q0, Q1, Q2, Q3, Q4, Q5]), "radius" : 3 * mm, "tangentPropagation" : true, "allowEdgeOverflow" : false});
        }
        {
            var Q0;
            Q0=makeQuery(id+"F1.opExtrude","CAP_EDGE",EDGE,{"disambiguationData":[OSD([sQuery(id+"F0.wireOp",EDGE,"E1.bottom")])],"isStart":false});
            fillet(context, id + "F15", {"entities" : qUnion([Q0]), "radius" : 2 * mm, "tangentPropagation" : true, "allowEdgeOverflow" : false});
        }
        {
            var Q0;
            {var subQ0=sQuery(id+"F0.wireOp",EDGE,"E22.filletArc");var subQ1=sQuery(id+"F0.wireOp",EDGE,"E7");var subQ2=sQuery(id+"F0.wireOp",EDGE,"E6");var subQ3=sQuery(id+"F0.wireOp",EDGE,"E5");var subQ4=sQuery(id+"F0.wireOp",EDGE,"E4");var subQ5=sQuery(id+"F0.wireOp",EDGE,"E1.bottom");var subQ6=sQuery(id+"F0.wireOp",EDGE,"E21.filletArc");var subQ7=sQuery(id+"F0.wireOp",EDGE,"E1.top");var subQ8=sQuery(id+"F0.wireOp",EDGE,"E1.left");var subQ9=sQuery(id+"F0.wireOp",EDGE,"E1.right");var subQ10=sQuery(id+"F0.wireOp",EDGE,"E23.filletArc");var subQ11=sQuery(id+"F0.wireOp",EDGE,"E24.filletArc");Q0=makeQuery(id+"F2.boolean.opBoolean","SPLIT",FACE,{"disambiguationData":[TD([makeQuery(id+"F1.opExtrude","SWEPT_FACE",FACE,{"disambiguationData":[OSD([subQ5])]})])],"derivedFrom":makeQuery(id+"F1.opExtrude","CAP_FACE",FACE,{"disambiguationData":[OSD([subQ5,subQ7,subQ8,subQ9,subQ4,subQ3,subQ2,subQ1,subQ6,subQ0,subQ10,subQ11])],"isStart":true})});}
            var sketch = newSketch(context, id + "F16", { "sketchPlane" : qUnion([Q0])});
            skCircle(sketch, "E79", {"center": v(0, 120) * mm, "radius": 6 * mm});
            skPoint(sketch, "E79.centerSnap0", {"position": v(0, 90) * mm});
            skLineSegment(sketch, "E80", {"start": v(-33, 90) * mm, "end": v(-15, 108) * mm});
            skLineSegment(sketch, "E81", {"start": v(-15, 108) * mm, "end": v(-15, 120) * mm});
            skArc(sketch, "E82", {"start": v(15, 120) * mm, "mid": v(0, 135) * mm, "end": v(-15, 120) * mm});
            skLineSegment(sketch, "E83", {"start": v(15, 120) * mm, "end": v(15, 108) * mm});
            skLineSegment(sketch, "E84", {"start": v(15, 108) * mm, "end": v(33, 90) * mm});
            skLineSegment(sketch, "E85", {"start": v(-80, 0) * mm, "end": v(80, 0) * mm, "construction": true});
            skArc(sketch, "E86.MirrorCS", {"start": v(15, -120) * mm, "mid": v(0, -135) * mm, "end": v(-15, -120) * mm});
            skLineSegment(sketch, "E87.MirrorCS", {"start": v(15, -120) * mm, "end": v(15, -108) * mm});
            skLineSegment(sketch, "E88.MirrorCS", {"start": v(-15, -108) * mm, "end": v(-15, -120) * mm});
            skCircle(sketch, "E89.MirrorC", {"center": v(0, -120) * mm, "radius": 6 * mm});
            skLineSegment(sketch, "E90.MirrorCS", {"start": v(15, -108) * mm, "end": v(33, -90) * mm});
            skLineSegment(sketch, "E91.MirrorCS", {"start": v(-33, -90) * mm, "end": v(-15, -108) * mm});
            skPoint(sketch, "E92.MirrorP", {"position": v(0, -90) * mm});
            skSolve(sketch);
        }
        {
            var Q0;
            Q0=makeQuery(id+"F16.imprint","IMPRINT",FACE,{"disambiguationData":[TD([[makeQuery(id+"F16.imprint","IMPRINT",EDGE,{"derivedFrom":sQuery(id+"F16.wireOp",EDGE,"E79")}),-1.0]])]});
            var Q1;
            Q1=makeQuery(id+"F16.imprint","IMPRINT",FACE,{"disambiguationData":[TD([[makeQuery(id+"F16.imprint","IMPRINT",EDGE,{"derivedFrom":sQuery(id+"F16.wireOp",EDGE,"E88.MirrorCS")}),1.0]])]});
            var Q2;
            Q2=makeQuery(id+"F16.imprint","IMPRINT",FACE,{"disambiguationData":[TD([[makeQuery(id+"F16.imprint","IMPRINT",EDGE,{"derivedFrom":makeQuery(id+"F1.opExtrude","CAP_EDGE",EDGE,{"disambiguationData":[OSD([sQuery(id+"F0.wireOp",EDGE,"E1.left")])],"isStart":true})}),-1.0]])]});
            var Q3;
            Q3=makeQuery(id+"F2.opExtrude","CAP_FACE",FACE,{"disambiguationData":[OSD([sQuery(id+"F0.wireOp",EDGE,"E12"),sQuery(id+"F0.wireOp",EDGE,"E13"),sQuery(id+"F0.wireOp",EDGE,"E14"),sQuery(id+"F0.wireOp",EDGE,"E15"),sQuery(id+"F0.wireOp",EDGE,"E17.filletArc"),sQuery(id+"F0.wireOp",EDGE,"E18.filletArc"),sQuery(id+"F0.wireOp",EDGE,"E19.filletArc"),sQuery(id+"F0.wireOp",EDGE,"E20.filletArc"),sQuery(id+"F0.wireOp",EDGE,"E25.0"),sQuery(id+"F0.wireOp",EDGE,"E25.1"),sQuery(id+"F0.wireOp",EDGE,"E25.2"),sQuery(id+"F0.wireOp",EDGE,"E25.3"),sQuery(id+"F0.wireOp",EDGE,"E25.4"),sQuery(id+"F0.wireOp",EDGE,"E25.5"),sQuery(id+"F0.wireOp",EDGE,"E25.6"),sQuery(id+"F0.wireOp",EDGE,"E25.7")])],"isStart":false});
            extrude(context, id + "F17", {"entities" : qUnion([Q0, Q1, Q2]), "endBound" : BoundingType.UP_TO_SURFACE, "endBoundEntityFace" : qUnion([Q3]), "depth" : 25 * mm});
        }
    });
